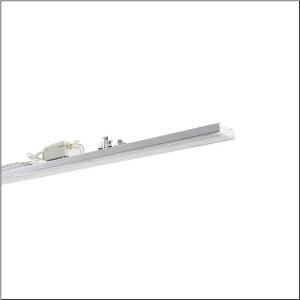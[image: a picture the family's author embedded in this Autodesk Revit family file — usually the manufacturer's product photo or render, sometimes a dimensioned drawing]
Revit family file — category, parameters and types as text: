
# Revit family: licross_21_recessed_ho_52te18dn4e5m
name_source: partatom
category: Lighting Fixtures
units: mm (PartAtom-declared; Revit-internal decimal feet)

## family parameters
Cut with Voids When Loaded = No
Host = Face
Light Source = No
Part Type = Normal
Room Calculation Point = No
Round Connector Dimension = Use Diameter
Shared = No

## types (1)
- --- (1 x LED, 14850 lm, 84.6 W, 4000K)
    Apparent Load = 85 VA
    CIE Flux Codes = 75 94 99 100 100
    Color Rendering = 80
    Color Temperature = 4000K
    Default Elevation = 1800 mm
    Description = Licross 21 Recessed HO, luminaire insert, of sheet steel, galvanised, coil coated, white, length: 1.500mm, width: 66mm, height: 67mm, LED rated luminous flux: 14.850lm, light colour: 840, SDCM (Standard Deviation of Colour Matching)MacAdam ≤ 3 SDCM (initial), control gear: DALI 2, with plug, 5-pole, with phase selection, mains connection: 220..240V, AC, 50/60Hz, rated input power: 85W, internal wiring halogen-free, primary light control with lens, of plastic, primary optical cover: cover, of PMMA, light emission: direct distribution, primary light characteristic: symmetric, protection rating (complete): IP54, insulation class (complete): insulation class I (protective earthing), certification: CE, ENEC, VDE, UKCA, protection symbol: D if used in an environment with non-conductive dust loads with corresponding accessories, impact resistance: IK06, permissible ambient temperature for indoor applications: -25..+30°C, corresponds to IFS (International Featured Standards) requirements for safety and quality in the food industry, reducing of maximum allowable ambient temperature of 5°C with ceiling mounting, LABS conformity tested according to VDMA 24364:2018-05, The light source and the operating device comply with the requirements of the Ecodesign Regulation (EU) 2019/2020 and are replaceable in accordance with this regulation, packaging unit: 1 piece
    Height = 58 mm
    Lamp = 1 x LED
    Lamp Light Flux = 14850 lm
    Lamp Power = 84.6 W
    Lamp count = 1
    Length = 1500 mm
    Luminous efficacy = 176 lm/W
    Manufacturer = Siteco
    ModVariant = No
    Model = 52TE18DN4E5M
    Mounting Place = Ceiling
    Mounting Type = Pendant
    Number of Poles = 1
    OnlyDefault = Yes
    Power Factor = 1
    Product Name = Licross 21 Recessed HO
    Product group = luminaire insert | ceiling pendant
    ProductGroupID = 901
    Protection Class = Protection class I
    Protection Degree = IP 54
    RLX_Detail_Level = 1
    RLX_Emergency_Light_Flux = 0 lm
    RLX_Emergency_Type = 0
    RLX_Emergency_Type_DB = No
    RlxData = <blob elided: 24985 chars, md5=4bb780ac>
    Socket = socket
    Standby Power = 0 W
    System Light Flux = 14850 lm
    System Power = 85 W
    Type Comments = factory setting: luminous flux: 100 % | dim-lin: 254 | 484 mA
    Type Image = l_1296930.jpg
    URL = http://relux.com
    VarID = @adj_127433
    Voltage = 0 V
    Weight = 0.00 kg
    Width = 66 mm

## geometry (parser evidence)
native form markers: Blend x4, Sweep x11
no freeform markers — native parametric forms only
